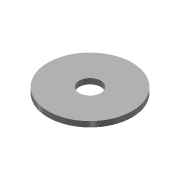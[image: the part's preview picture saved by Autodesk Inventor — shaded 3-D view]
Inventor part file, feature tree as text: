
AUTODESK INVENTOR PART (.ipt)
format: ipt  version: 2016 SP2 (Build 200236200, 236)  size: 80,384 bytes
history: native  units: in
note: dims shown in document units (in); Inventor stores cm internally (conversion verified against a paired STEP export)
features: extrude x1, sketch x1
ambient origin geometry x8: Origin, YZ Plane, XZ Plane, XY Plane, X Axis, Y Axis, Z Axis, Center Point
bodies: Solid1 (feature_tree)
feature tree (2):
  extrude  "Extrusion1"  Depth=0.1in
  sketch  "Sketch1"  dims[d1=0.3937in d2=1.5354in d3=0.1in d4=0.0in]
